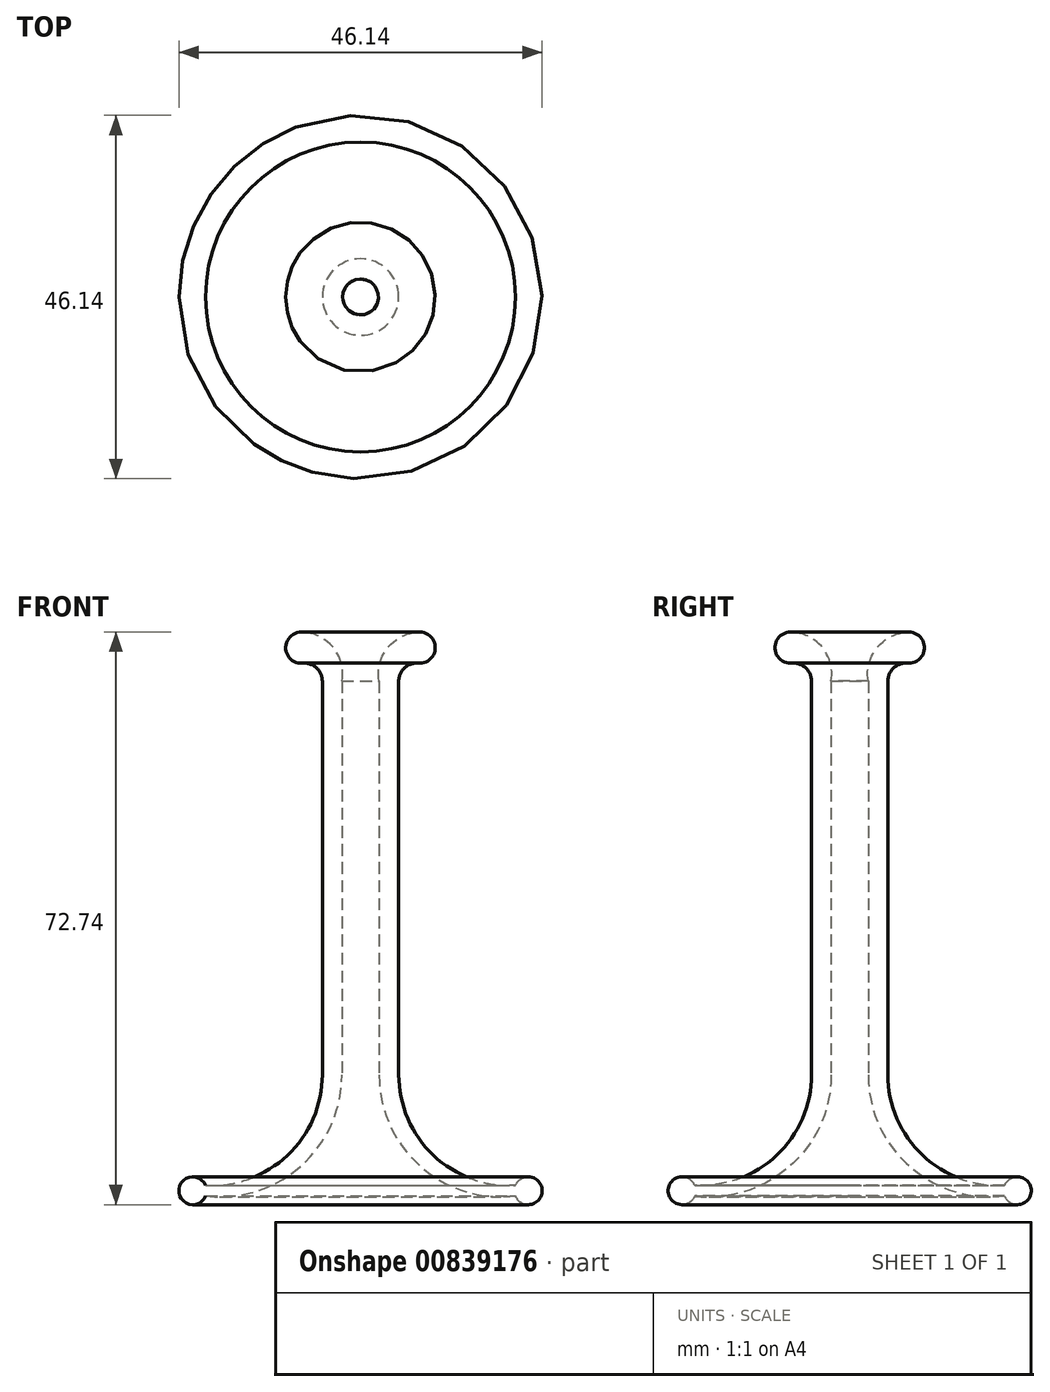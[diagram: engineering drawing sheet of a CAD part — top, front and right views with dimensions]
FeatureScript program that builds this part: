
annotation { "Feature Type Name" : "Feature", "Feature Type Description" : "" }
export const myFeature = defineFeature(function(context is Context, id is Id, definition is map)
    precondition{}
    {
        {
            var Q0;
            Q0=qCreatedBy(makeId("Front.planeOp"),FACE);
            var sketch = newSketch(context, id + "F0", { "sketchPlane" : qUnion([Q0])});
            skLineSegment(sketch, "E0", {"start": v(-2.65, 0) * mm, "end": v(-2.65, 50) * mm});
            skLineSegment(sketch, "E1", {"start": v(2.35, 0) * mm, "end": v(2.35, 50) * mm});
            skLineSegment(sketch, "E2", {"start": v(-5.15, 0) * mm, "end": v(-5.15, 50) * mm});
            skLineSegment(sketch, "E3", {"start": v(4.85, 0) * mm, "end": v(4.85, 50) * mm});
            skArc(sketch, "E4", {"start": v(4.85, 50) * mm, "mid": v(5.6, 51.7) * mm, "end": v(7.35, 52.29) * mm});
            skArc(sketch, "E5", {"start": v(7.35, 52.29) * mm, "mid": v(9.5, 54.19) * mm, "end": v(7.48, 56.23) * mm});
            skArc(sketch, "E6", {"start": v(7.48, 56.23) * mm, "mid": v(3.49, 54.29) * mm, "end": v(2.35, 50) * mm});
            skArc(sketch, "E7", {"start": v(4.85, 0) * mm, "mid": v(9.24, -10.22) * mm, "end": v(19.68, -14.07) * mm});
            skArc(sketch, "E8", {"start": v(2.35, 0) * mm, "mid": v(7.56, -11.6) * mm, "end": v(19.68, -15.42) * mm});
            skArc(sketch, "E9", {"start": v(19.68, -15.42) * mm, "mid": v(23.07, -14.74) * mm, "end": v(19.68, -14.07) * mm});
            skLineSegment(sketch, "E10", {"start": v(0, 0) * mm, "end": v(0, 50.44) * mm});
            skSolve(sketch);
        }
        {
            var Q0;
            Q0 = qSketchRegion(id + "F0", true);
            var Q1;
            Q1=sQuery(id+"F0.wireOp",EDGE,"E10");
            revolve(context, id + "F1", {"surfaceOperationType" : NewSurfaceOperationType.NEW, "entities" : qUnion([Q0]), "axis" : qUnion([Q1]), "revolveType" : RevolveType.FULL});
        }
    });
